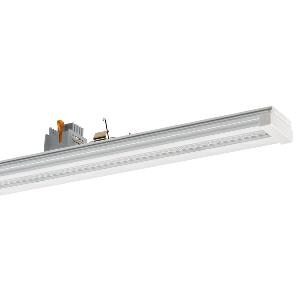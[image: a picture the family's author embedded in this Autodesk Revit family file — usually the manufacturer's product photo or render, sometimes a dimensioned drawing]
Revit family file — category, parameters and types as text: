
# Revit family: conveo_-_cvg_8000_840_xn-l_da_7_226848399-00804978_4921
name_source: partatom
category: Lighting Fixtures
units: mm (PartAtom-declared; Revit-internal decimal feet)

## family parameters
Cut with Voids When Loaded = No
Host = Face
Light Source = No
Part Type = Normal
Room Calculation Point = No
Round Connector Dimension = Use Diameter
Shared = No

## types (1)
- CONVEO - CVG 8000/840/xN-L/DA/7 (1 x LED, 8450 lm, 4000K)
    Apparent Load = 51 VA
    Approval mark = CE
    CIE Flux Codes = 84 95 99 100 100
    Color Rendering = 80-89
    Color Temperature = 4000K
    Control Gear = Electronic ballast
    Default Elevation = 1800 mm
    Description = CVG 8000/840/xN-L/DA/7|Continuous-row system|light source: LED|work equipment: Adjustable electronic ballast, digital DALI|connected load: 220-240 V, 50-60 Hz|Power consumption: approx. 51 W|luminous flux: 8450 lm|luminous efficacy: 165 lm/W|colour temperature: Cold white, ca. 4000 K|color rendering index (CRI): >= 80|chromaticity tolerance:  3 SDCM|System of protection: IP 54|class of protection: I|technology: Continuously dimmable|luminaire body|material: Aluminium|surface: Powder coatet|colour: White|lamp cover: Acrylic (PMMA), Satine|weight (net): approx. 1.9 kg|Fastening: Available separately|maximum ambient temperature: 42 ░C|glare control: Lens optics|Approval mark: VDE - ENEC|
    Frequency = 50 Hz
    Height = 70 mm
    Lamp = 1 x LED
    Lamp Light Flux = 8450 lm
    Lamp count = 1
    Length = 1500 mm
    Luminous efficacy = 166 lm/W
    Manufacturer = Waldmann
    ModVariant = No
    Model = 226848399-00804978
    Mounting Place = Ceiling
    Mounting Type = Pendant
    Number of Poles = 1
    OnlyDefault = Yes
    Power Factor = 1
    Product Name = CONVEO - CVG 8000/840/xN-L/DA/7
    Product group = Continuous-row system (industry)
    ProductGroupID = 301
    Protection Class = Protection class I
    Protection Degree = IP 54
    RLX_Detail_Level = 1
    RlxData = <blob elided: 101069 chars, md5=80b9b24f>
    Socket = socket
    Standby Power = 0 W
    System Light Flux = 8450 lm
    System Power = 51 W
    Type Comments = Product without accessories
    Type Image = 226848259-00804964_1l7.jpg
    URL = http://relux.com
    VarID = ---
    Voltage = 230 V
    Voltage Range = 220-240 V
    Weight = 0.00 kg
    Width = 64 mm

## geometry (parser evidence)
native form markers: Blend x4, Sweep x9
no freeform markers — native parametric forms only
